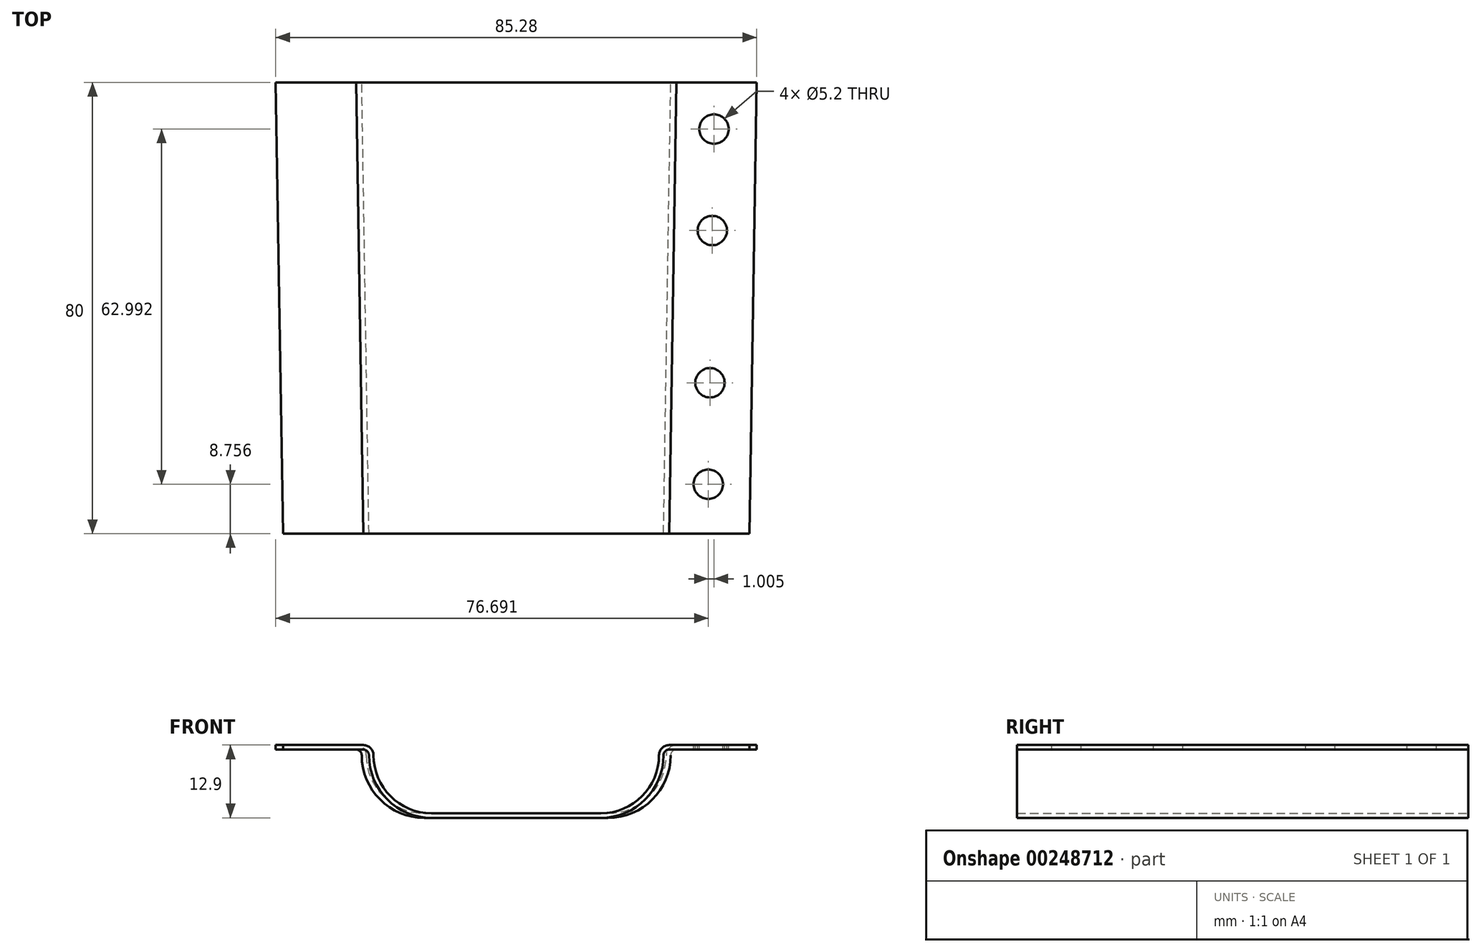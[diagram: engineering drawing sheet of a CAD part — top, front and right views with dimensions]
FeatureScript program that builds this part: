
annotation { "Feature Type Name" : "Feature", "Feature Type Description" : "" }
export const myFeature = defineFeature(function(context is Context, id is Id, definition is map)
    precondition{}
    {
        {
            var Q0;
            Q0=qCreatedBy(makeId("Front.planeOp"),FACE);
            var sketch = newSketch(context, id + "F0", { "sketchPlane" : qUnion([Q0])});
            skLineSegment(sketch, "E0", {"start": v(-41.36, 12.1) * mm, "end": v(-27.11, 12.1) * mm});
            skArc(sketch, "E1", {"start": v(-27.11, 12.1) * mm, "mid": v(-25.84, 11.57) * mm, "end": v(-25.31, 10.3) * mm});
            skArc(sketch, "E2", {"start": v(-25.31, 10.3) * mm, "mid": v(-22.3, 3.02) * mm, "end": v(-15.01, 0) * mm});
            skLineSegment(sketch, "E3.1", {"start": v(-41.36, 11.3) * mm, "end": v(-27.11, 11.3) * mm});
            skArc(sketch, "E3.2", {"start": v(-26.11, 10.3) * mm, "mid": v(-22.86, 2.45) * mm, "end": v(-15.01, -0.8) * mm});
            skPoint(sketch, "E4.visualSharp", {"position": v(-26.07, 11.3) * mm});
            skArc(sketch, "E4.filletArc", {"start": v(-26.11, 10.3) * mm, "mid": v(-26.4, 11) * mm, "end": v(-27.11, 11.3) * mm});
            skLineSegment(sketch, "E5", {"start": v(-41.36, 12.1) * mm, "end": v(-41.36, 11.3) * mm});
            skPoint(sketch, "E6", {"position": v(0, 0) * mm});
            skLineSegment(sketch, "E7", {"start": v(-15.01, 0) * mm, "end": v(15.01, 0) * mm});
            skLineSegment(sketch, "E8", {"start": v(0, 0) * mm, "end": v(0, -8.94) * mm, "construction": true});
            skArc(sketch, "E9.MirrorCS", {"start": v(26.11, 10.3) * mm, "mid": v(26.4, 11) * mm, "end": v(27.11, 11.3) * mm});
            skArc(sketch, "E10.MirrorCS", {"start": v(27.11, 12.1) * mm, "mid": v(25.84, 11.57) * mm, "end": v(25.31, 10.3) * mm});
            skLineSegment(sketch, "E11.MirrorCS", {"start": v(41.36, 12.1) * mm, "end": v(41.36, 11.3) * mm});
            skPoint(sketch, "E12.MirrorP", {"position": v(26.07, 11.3) * mm});
            skLineSegment(sketch, "E13.MirrorCS", {"start": v(41.36, 11.3) * mm, "end": v(27.11, 11.3) * mm});
            skLineSegment(sketch, "E14.MirrorCS", {"start": v(41.36, 12.1) * mm, "end": v(27.11, 12.1) * mm});
            skArc(sketch, "E15.MirrorCS", {"start": v(26.11, 10.3) * mm, "mid": v(22.86, 2.45) * mm, "end": v(15.01, -0.8) * mm});
            skArc(sketch, "E16.MirrorCS", {"start": v(25.31, 10.3) * mm, "mid": v(22.3, 3.02) * mm, "end": v(15.01, 0) * mm});
            skLineSegment(sketch, "E17", {"start": v(-15.01, -0.8) * mm, "end": v(15.01, -0.8) * mm});
            skSolve(sketch);
        }
        {
            var Q0;
            Q0=qCreatedBy(makeId("Front.planeOp"),FACE);
            cPlane(context, id + "F1", {"entities" : qUnion([Q0]), "cplaneType" : CPlaneType.OFFSET, "offset" : 80 * mm, "oppositeDirection" : true, "width" : 150 * mm, "height" : 150 * mm});
        }
        {
            var Q0;
            Q0=qCreatedBy(id+"F1.planeOp",FACE);
            var sketch = newSketch(context, id + "F2", { "sketchPlane" : qUnion([Q0])});
            skLineSegment(sketch, "E18", {"start": v(-42.64, 12.1) * mm, "end": v(-28.39, 12.1) * mm});
            skArc(sketch, "E19", {"start": v(-28.39, 12.1) * mm, "mid": v(-27.12, 11.57) * mm, "end": v(-26.59, 10.3) * mm});
            skArc(sketch, "E20", {"start": v(-26.59, 10.3) * mm, "mid": v(-23.57, 3.02) * mm, "end": v(-16.29, 0) * mm});
            skArc(sketch, "E21", {"start": v(16.29, 0) * mm, "mid": v(23.57, 3.02) * mm, "end": v(26.59, 10.3) * mm});
            skArc(sketch, "E22", {"start": v(26.59, 10.3) * mm, "mid": v(27.12, 11.57) * mm, "end": v(28.39, 12.1) * mm});
            skLineSegment(sketch, "E23", {"start": v(28.39, 12.1) * mm, "end": v(42.64, 12.1) * mm});
            skLineSegment(sketch, "E24.0", {"start": v(28.39, 11.3) * mm, "end": v(42.64, 11.3) * mm});
            skLineSegment(sketch, "E24.1", {"start": v(-42.64, 11.3) * mm, "end": v(-28.39, 11.3) * mm});
            skArc(sketch, "E24.2", {"start": v(-27.39, 10.3) * mm, "mid": v(-24.14, 2.45) * mm, "end": v(-16.29, -0.8) * mm});
            skArc(sketch, "E24.4", {"start": v(16.29, -0.8) * mm, "mid": v(24.14, 2.45) * mm, "end": v(27.39, 10.3) * mm});
            skArc(sketch, "E25.filletArc", {"start": v(-27.39, 10.3) * mm, "mid": v(-27.68, 11) * mm, "end": v(-28.39, 11.3) * mm});
            skArc(sketch, "E26.filletArc", {"start": v(28.39, 11.3) * mm, "mid": v(27.68, 11) * mm, "end": v(27.39, 10.3) * mm});
            skLineSegment(sketch, "E27", {"start": v(42.64, 12.1) * mm, "end": v(42.64, 11.3) * mm});
            skLineSegment(sketch, "E28", {"start": v(-42.64, 12.1) * mm, "end": v(-42.64, 11.3) * mm});
            skLineSegment(sketch, "E29", {"start": v(-16.29, 0) * mm, "end": v(16.29, 0) * mm});
            skPoint(sketch, "E30", {"position": v(0, 0) * mm});
            skLineSegment(sketch, "E31", {"start": v(-16.29, -0.8) * mm, "end": v(16.29, -0.8) * mm});
            skSolve(sketch);
        }
        {
            var Q0;
            Q0 = qSketchRegion(id + "F0", true);
            var Q1;
            Q1 = qSketchRegion(id + "F2", true);
            loft(context, id + "F3", {"sheetProfilesArray" : [{ "sheetProfileEntities" : qUnion([Q0]) }, { "sheetProfileEntities" : qUnion([Q1]) }]});
        }
        {
            var Q0;
            Q0=makeQuery(id+"F3.opLoft","SWEPT_FACE",FACE,{"disambiguationData":[OSD([sQuery(id+"F0.wireOp",EDGE,"E10.MirrorCS"),sQuery(id+"F0.wireOp",EDGE,"E11.MirrorCS"),sQuery(id+"F0.wireOp",EDGE,"E14.MirrorCS"),sQuery(id+"F2.wireOp",EDGE,"E22"),sQuery(id+"F2.wireOp",EDGE,"E23"),sQuery(id+"F2.wireOp",EDGE,"E27")])]});
            var sketch = newSketch(context, id + "F4", { "sketchPlane" : qUnion([Q0])});
            skLineSegment(sketch, "E32.0", {"start": v(41.36, 0) * mm, "end": v(42.64, 80) * mm, "construction": true});
            skLineSegment(sketch, "E33.0", {"start": v(33.92, 0.25) * mm, "end": v(35.2, 80.25) * mm, "construction": true});
            skLineSegment(sketch, "E34", {"start": v(34.55, 40.25) * mm, "end": v(59.07, 39.86) * mm, "construction": true});
            skLineSegment(sketch, "E35.0", {"start": v(34.34, 26.75) * mm, "end": v(58.86, 26.36) * mm});
            skLineSegment(sketch, "E36.0", {"start": v(34.77, 53.75) * mm, "end": v(59.29, 53.36) * mm});
            skLineSegment(sketch, "E37.0", {"start": v(34.05, 8.76) * mm, "end": v(58.57, 8.37) * mm});
            skLineSegment(sketch, "E38.0", {"start": v(35.06, 71.75) * mm, "end": v(59.58, 71.36) * mm});
            skCircle(sketch, "E39", {"center": v(35.06, 71.75) * mm, "radius": 2.6 * mm});
            skCircle(sketch, "E40", {"center": v(34.77, 53.75) * mm, "radius": 2.6 * mm});
            skCircle(sketch, "E41", {"center": v(34.34, 26.75) * mm, "radius": 2.6 * mm});
            skCircle(sketch, "E42", {"center": v(34.05, 8.76) * mm, "radius": 2.6 * mm});
            skLineSegment(sketch, "E43", {"start": v(0, 80.95) * mm, "end": v(0, 0) * mm, "construction": true});
            skCircle(sketch, "E44.MirrorC", {"center": v(-35.06, 71.75) * mm, "radius": 2.6 * mm});
            skCircle(sketch, "E45.MirrorC", {"center": v(-34.77, 53.75) * mm, "radius": 2.6 * mm});
            skCircle(sketch, "E46.MirrorC", {"center": v(-34.34, 26.75) * mm, "radius": 2.6 * mm});
            skCircle(sketch, "E47.MirrorC", {"center": v(-34.05, 8.76) * mm, "radius": 2.6 * mm});
            skSolve(sketch);
        }
        {
            var Q0;
            Q0=makeQuery(id+"F4.imprint","IMPRINT",FACE,{"disambiguationData":[TD([[makeQuery(id+"F4.imprint","IMPRINT",EDGE,{"derivedFrom":sQuery(id+"F4.wireOp",EDGE,"E44.MirrorC")}),-1.0]])]});
            var Q1;
            Q1=makeQuery(id+"F4.imprint","IMPRINT",FACE,{"disambiguationData":[TD([[makeQuery(id+"F4.imprint","IMPRINT",EDGE,{"derivedFrom":sQuery(id+"F4.wireOp",EDGE,"E45.MirrorC")}),-1.0]])]});
            var Q2;
            Q2=makeQuery(id+"F4.imprint","IMPRINT",FACE,{"disambiguationData":[TD([[makeQuery(id+"F4.imprint","IMPRINT",EDGE,{"derivedFrom":sQuery(id+"F4.wireOp",EDGE,"E46.MirrorC")}),-1.0]])]});
            var Q3;
            Q3=makeQuery(id+"F4.imprint","IMPRINT",FACE,{"disambiguationData":[TD([[makeQuery(id+"F4.imprint","IMPRINT",EDGE,{"derivedFrom":sQuery(id+"F4.wireOp",EDGE,"E47.MirrorC")}),-1.0]])]});
            var Q4;
            Q4=makeQuery(id+"F4.imprint","IMPRINT",FACE,{"disambiguationData":[TD([[makeQuery(id+"F4.imprint","IMPRINT",EDGE,{"derivedFrom":sQuery(id+"F4.wireOp",EDGE,"E42")}),1.0]])]});
            var Q5;
            Q5=makeQuery(id+"F4.imprint","IMPRINT",FACE,{"disambiguationData":[TD([[makeQuery(id+"F4.imprint","IMPRINT",EDGE,{"derivedFrom":sQuery(id+"F4.wireOp",EDGE,"E41")}),1.0]])]});
            var Q6;
            Q6=makeQuery(id+"F4.imprint","IMPRINT",FACE,{"disambiguationData":[TD([[makeQuery(id+"F4.imprint","IMPRINT",EDGE,{"derivedFrom":sQuery(id+"F4.wireOp",EDGE,"E40")}),1.0]])]});
            var Q7;
            Q7=makeQuery(id+"F4.imprint","IMPRINT",FACE,{"disambiguationData":[TD([[makeQuery(id+"F4.imprint","IMPRINT",EDGE,{"derivedFrom":sQuery(id+"F4.wireOp",EDGE,"E39")}),1.0]])]});
            extrude(context, id + "F5", {"entities" : qUnion([Q0, Q1, Q2, Q3, Q4, Q5, Q6, Q7]), "operationType" : NewBodyOperationType.REMOVE, "endBound" : BoundingType.THROUGH_ALL, "oppositeDirection" : true, "depth" : 25 * mm});
        }
    });
